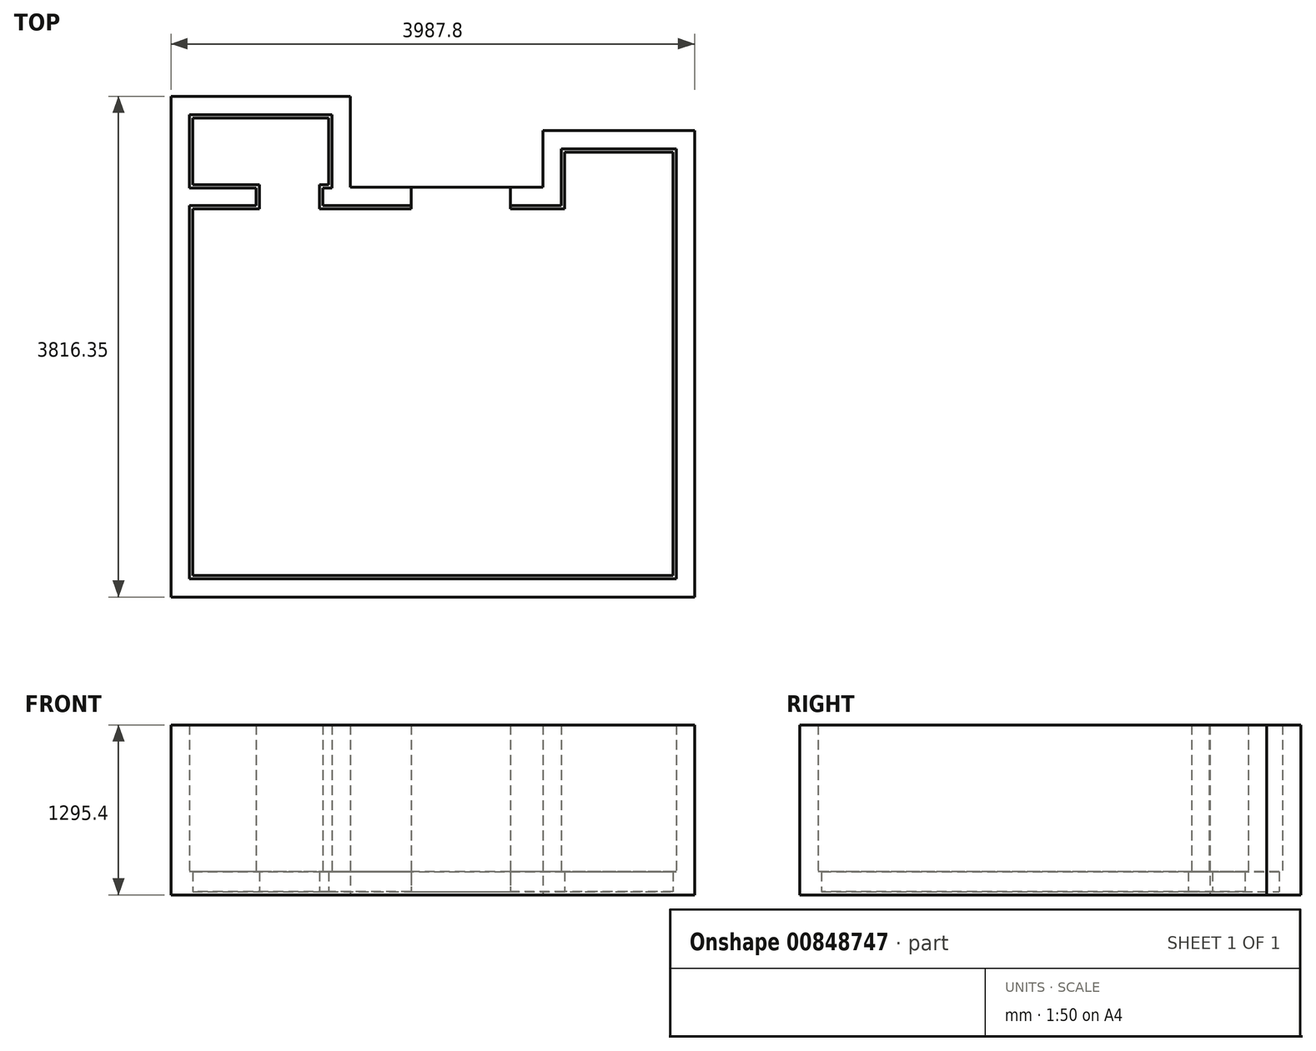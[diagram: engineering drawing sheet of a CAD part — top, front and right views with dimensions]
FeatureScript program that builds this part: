
annotation { "Feature Type Name" : "Feature", "Feature Type Description" : "" }
export const myFeature = defineFeature(function(context is Context, id is Id, definition is map)
    precondition{}
    {
        {
            var Q0;
            Q0=qCreatedBy(makeId("Top.planeOp"),FACE);
            var sketch = newSketch(context, id + "F0", { "sketchPlane" : qUnion([Q0])});
            skLineSegment(sketch, "E0", {"start": v(70.5, 706.89) * mm, "end": v(743.6, 706.89) * mm});
            skLineSegment(sketch, "E1", {"start": v(743.6, 706.89) * mm, "end": v(1499.26, 706.89) * mm, "construction": true});
            skLineSegment(sketch, "E2", {"start": v(1499.26, 706.89) * mm, "end": v(1886.6, 706.89) * mm});
            skLineSegment(sketch, "E3", {"start": v(1886.6, 706.89) * mm, "end": v(1886.6, 1138.69) * mm});
            skLineSegment(sketch, "E4", {"start": v(1886.6, 1138.69) * mm, "end": v(2762.9, 1138.69) * mm});
            skLineSegment(sketch, "E5", {"start": v(2762.9, 1138.69) * mm, "end": v(2762.9, -2137.91) * mm});
            skLineSegment(sketch, "E6", {"start": v(70.5, 706.89) * mm, "end": v(-437.5, 706.89) * mm, "construction": true});
            skLineSegment(sketch, "E7", {"start": v(-437.5, 706.89) * mm, "end": v(-945.5, 706.89) * mm});
            skLineSegment(sketch, "E8", {"start": v(-945.5, 706.89) * mm, "end": v(-945.5, -2137.91) * mm});
            skLineSegment(sketch, "E9", {"start": v(2762.9, -2137.91) * mm, "end": v(-945.5, -2137.91) * mm});
            skLineSegment(sketch, "E10", {"start": v(70.5, 706.89) * mm, "end": v(70.5, 840.24) * mm});
            skLineSegment(sketch, "E11", {"start": v(70.5, 840.24) * mm, "end": v(140.36, 840.24) * mm});
            skLineSegment(sketch, "E12", {"start": v(140.36, 840.24) * mm, "end": v(140.36, 1399.04) * mm});
            skLineSegment(sketch, "E13", {"start": v(-437.5, 706.89) * mm, "end": v(-437.5, 840.24) * mm});
            skLineSegment(sketch, "E14", {"start": v(-437.5, 840.24) * mm, "end": v(-945.5, 840.24) * mm});
            skLineSegment(sketch, "E15", {"start": v(-945.5, 840.24) * mm, "end": v(-945.5, 1399.04) * mm});
            skLineSegment(sketch, "E16", {"start": v(140.36, 1399.04) * mm, "end": v(-945.5, 1399.04) * mm});
            skLineSegment(sketch, "E17.0", {"start": v(-1085.2, 1538.74) * mm, "end": v(-1085.2, -2277.61) * mm});
            skLineSegment(sketch, "E17.1", {"start": v(2902.6, -2277.61) * mm, "end": v(-1085.2, -2277.61) * mm});
            skLineSegment(sketch, "E17.2", {"start": v(2902.6, 1278.39) * mm, "end": v(2902.6, -2277.61) * mm});
            skLineSegment(sketch, "E17.4", {"start": v(1499.26, 846.59) * mm, "end": v(1746.9, 846.59) * mm});
            skLineSegment(sketch, "E17.5", {"start": v(1746.9, 846.59) * mm, "end": v(1746.9, 1278.39) * mm});
            skLineSegment(sketch, "E17.6", {"start": v(1746.9, 1278.39) * mm, "end": v(2902.6, 1278.39) * mm});
            skLineSegment(sketch, "E18.1", {"start": v(280.06, 1538.74) * mm, "end": v(-1085.2, 1538.74) * mm});
            skLineSegment(sketch, "E18.2", {"start": v(280.06, 846.59) * mm, "end": v(280.06, 1538.74) * mm});
            skLineSegment(sketch, "E19", {"start": v(743.6, 846.59) * mm, "end": v(280.06, 846.59) * mm});
            skLineSegment(sketch, "E20", {"start": v(1499.26, 706.89) * mm, "end": v(1499.26, 846.59) * mm});
            skLineSegment(sketch, "E21", {"start": v(743.6, 706.89) * mm, "end": v(743.6, 846.59) * mm});
            skSolve(sketch);
        }
        {
            var Q0;
            Q0 = qSketchRegion(id + "F0", true);
            extrude(context, id + "F1", {"entities" : qUnion([Q0]), "depth" : 1270 * mm, "offsetDistance" : 25.4 * mm});
        }
        {
            var Q0;
            Q0=makeQuery(id+"F1.opExtrude","CAP_FACE",FACE,{"disambiguationData":[OSD([sQuery(id+"F0.wireOp",EDGE,"E0"),sQuery(id+"F0.wireOp",EDGE,"E2"),sQuery(id+"F0.wireOp",EDGE,"E3"),sQuery(id+"F0.wireOp",EDGE,"E4"),sQuery(id+"F0.wireOp",EDGE,"E5"),sQuery(id+"F0.wireOp",EDGE,"E7"),sQuery(id+"F0.wireOp",EDGE,"E8"),sQuery(id+"F0.wireOp",EDGE,"E9"),sQuery(id+"F0.wireOp",EDGE,"E10"),sQuery(id+"F0.wireOp",EDGE,"E11"),sQuery(id+"F0.wireOp",EDGE,"E12"),sQuery(id+"F0.wireOp",EDGE,"E13"),sQuery(id+"F0.wireOp",EDGE,"E14"),sQuery(id+"F0.wireOp",EDGE,"E15"),sQuery(id+"F0.wireOp",EDGE,"E16"),sQuery(id+"F0.wireOp",EDGE,"E17.0"),sQuery(id+"F0.wireOp",EDGE,"E17.1"),sQuery(id+"F0.wireOp",EDGE,"E17.2"),sQuery(id+"F0.wireOp",EDGE,"E17.4"),sQuery(id+"F0.wireOp",EDGE,"E17.5"),sQuery(id+"F0.wireOp",EDGE,"E17.6"),sQuery(id+"F0.wireOp",EDGE,"E18.1"),sQuery(id+"F0.wireOp",EDGE,"E18.2"),sQuery(id+"F0.wireOp",EDGE,"E19"),sQuery(id+"F0.wireOp",EDGE,"E20"),sQuery(id+"F0.wireOp",EDGE,"E21")])],"isStart":true});
            var sketch = newSketch(context, id + "F2", { "sketchPlane" : qUnion([Q0])});
            skLineSegment(sketch, "E22.bottom", {"start": v(2902.6, 2277.61) * mm, "end": v(-1085.2, 2277.61) * mm});
            skLineSegment(sketch, "E22.top", {"start": v(280.06, -1538.74) * mm, "end": v(-1085.2, -1538.74) * mm});
            skLineSegment(sketch, "E22.left", {"start": v(2902.6, 2277.61) * mm, "end": v(2902.6, -1278.39) * mm});
            skLineSegment(sketch, "E22.right", {"start": v(-1085.2, 2277.61) * mm, "end": v(-1085.2, -1538.74) * mm});
            skLineSegment(sketch, "E23", {"start": v(2902.6, -1278.39) * mm, "end": v(1746.9, -1278.39) * mm});
            skLineSegment(sketch, "E24", {"start": v(1746.9, -1278.39) * mm, "end": v(1746.9, -846.59) * mm});
            skLineSegment(sketch, "E25", {"start": v(1746.9, -846.59) * mm, "end": v(280.06, -846.59) * mm});
            skLineSegment(sketch, "E26", {"start": v(280.06, -846.59) * mm, "end": v(280.06, -1538.74) * mm});
            skSolve(sketch);
        }
        {
            var Q0;
            Q0 = qSketchRegion(id + "F2", true);
            extrude(context, id + "F3", {"entities" : qUnion([Q0]), "operationType" : NewBodyOperationType.ADD, "depth" : 25.4 * mm, "offsetDistance" : 25.4 * mm});
        }
        {
            var Q0;
            Q0=makeQuery(id+"F3.opExtrude","CAP_FACE",FACE,{"disambiguationData":[OSD([sQuery(id+"F2.wireOp",EDGE,"E22.bottom"),sQuery(id+"F2.wireOp",EDGE,"E22.top"),sQuery(id+"F2.wireOp",EDGE,"E22.left"),sQuery(id+"F2.wireOp",EDGE,"E22.right"),sQuery(id+"F2.wireOp",EDGE,"E23"),sQuery(id+"F2.wireOp",EDGE,"E24"),sQuery(id+"F2.wireOp",EDGE,"E25"),sQuery(id+"F2.wireOp",EDGE,"E26")])],"isStart":true});
            var sketch = newSketch(context, id + "F4", { "sketchPlane" : qUnion([Q0])});
            skLineSegment(sketch, "E27.0", {"start": v(1886.6, 1138.69) * mm, "end": v(1886.6, 706.89) * mm});
            skLineSegment(sketch, "E27.1", {"start": v(2762.9, 1138.69) * mm, "end": v(1886.6, 1138.69) * mm});
            skLineSegment(sketch, "E27.2", {"start": v(2762.9, -2137.91) * mm, "end": v(2762.9, 1138.69) * mm});
            skLineSegment(sketch, "E27.3", {"start": v(-945.5, -2137.91) * mm, "end": v(2762.9, -2137.91) * mm});
            skLineSegment(sketch, "E27.4", {"start": v(-945.5, 706.89) * mm, "end": v(-945.5, -2137.91) * mm});
            skLineSegment(sketch, "E27.5", {"start": v(1886.6, 706.89) * mm, "end": v(1499.26, 706.89) * mm});
            skLineSegment(sketch, "E27.6", {"start": v(-437.5, 706.89) * mm, "end": v(-945.5, 706.89) * mm});
            skLineSegment(sketch, "E27.7", {"start": v(-437.5, 840.24) * mm, "end": v(-437.5, 706.89) * mm});
            skLineSegment(sketch, "E27.8", {"start": v(743.6, 706.89) * mm, "end": v(70.5, 706.89) * mm});
            skLineSegment(sketch, "E27.12", {"start": v(70.5, 706.89) * mm, "end": v(70.5, 840.24) * mm});
            skLineSegment(sketch, "E27.13", {"start": v(70.5, 840.24) * mm, "end": v(140.36, 840.24) * mm});
            skLineSegment(sketch, "E27.14", {"start": v(140.36, 840.24) * mm, "end": v(140.36, 1399.04) * mm});
            skLineSegment(sketch, "E27.15", {"start": v(140.36, 1399.04) * mm, "end": v(-945.5, 1399.04) * mm});
            skLineSegment(sketch, "E27.16", {"start": v(-945.5, 1399.04) * mm, "end": v(-945.5, 840.24) * mm});
            skLineSegment(sketch, "E27.17", {"start": v(-945.5, 840.24) * mm, "end": v(-437.5, 840.24) * mm});
            skLineSegment(sketch, "E28.0", {"start": v(1912, 1113.29) * mm, "end": v(1912, 681.49) * mm});
            skLineSegment(sketch, "E28.1", {"start": v(2737.5, 1113.29) * mm, "end": v(1912, 1113.29) * mm});
            skLineSegment(sketch, "E28.2", {"start": v(2737.5, -2112.51) * mm, "end": v(2737.5, 1113.29) * mm});
            skLineSegment(sketch, "E28.3", {"start": v(-920.1, -2112.51) * mm, "end": v(2737.5, -2112.51) * mm});
            skLineSegment(sketch, "E28.4", {"start": v(-920.1, 681.49) * mm, "end": v(-920.1, -2112.51) * mm});
            skLineSegment(sketch, "E28.5", {"start": v(1912, 681.49) * mm, "end": v(1499.26, 681.49) * mm});
            skLineSegment(sketch, "E28.6", {"start": v(-412.1, 681.49) * mm, "end": v(-920.1, 681.49) * mm});
            skLineSegment(sketch, "E28.7", {"start": v(-412.1, 865.64) * mm, "end": v(-412.1, 681.49) * mm});
            skLineSegment(sketch, "E28.8", {"start": v(743.6, 681.49) * mm, "end": v(45.1, 681.49) * mm});
            skLineSegment(sketch, "E28.12", {"start": v(45.1, 681.49) * mm, "end": v(45.1, 865.64) * mm});
            skLineSegment(sketch, "E28.13", {"start": v(45.1, 865.64) * mm, "end": v(114.96, 865.64) * mm});
            skLineSegment(sketch, "E28.14", {"start": v(114.96, 865.64) * mm, "end": v(114.96, 1373.64) * mm});
            skLineSegment(sketch, "E28.15", {"start": v(114.96, 1373.64) * mm, "end": v(-920.1, 1373.64) * mm});
            skLineSegment(sketch, "E28.16", {"start": v(-920.1, 1373.64) * mm, "end": v(-920.1, 865.64) * mm});
            skLineSegment(sketch, "E28.17", {"start": v(-920.1, 865.64) * mm, "end": v(-412.1, 865.64) * mm});
            skLineSegment(sketch, "E29", {"start": v(1499.26, 706.89) * mm, "end": v(1499.26, 681.49) * mm});
            skLineSegment(sketch, "E30", {"start": v(743.6, 706.89) * mm, "end": v(743.6, 681.49) * mm});
            skSolve(sketch);
        }
        {
            var Q0;
            Q0 = qSketchRegion(id + "F4", true);
            extrude(context, id + "F5", {"entities" : qUnion([Q0]), "operationType" : NewBodyOperationType.ADD, "depth" : 152.4 * mm, "offsetDistance" : 25.4 * mm});
        }
    });
